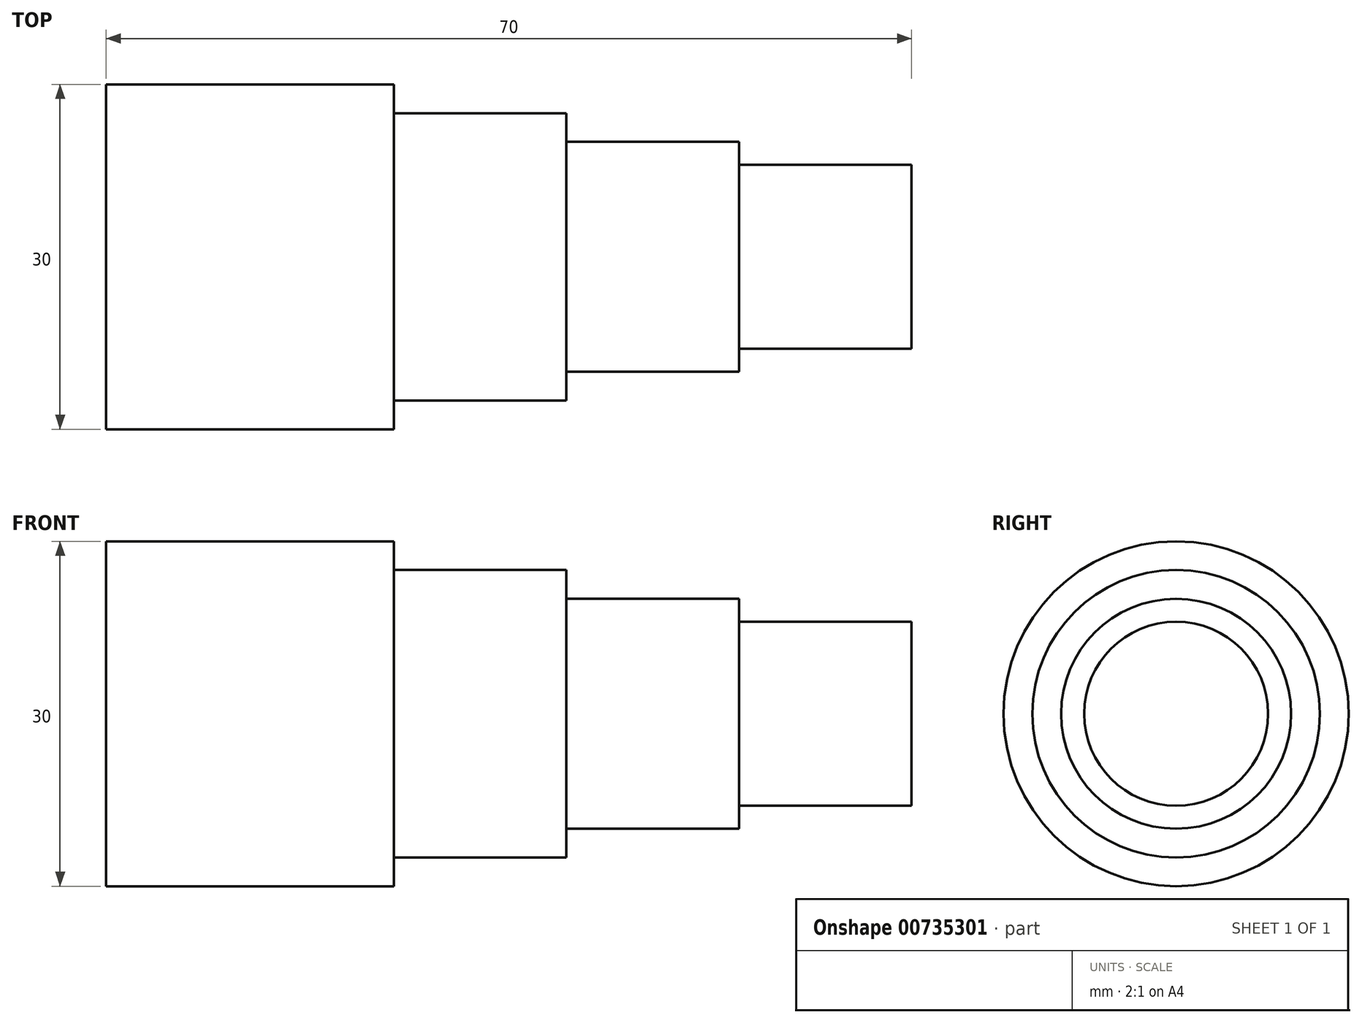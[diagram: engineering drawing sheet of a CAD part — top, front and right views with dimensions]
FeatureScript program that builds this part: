
annotation { "Feature Type Name" : "Feature", "Feature Type Description" : "" }
export const myFeature = defineFeature(function(context is Context, id is Id, definition is map)
    precondition{}
    {
        {
            var Q0;
            Q0=qCreatedBy(makeId("Right.planeOp"),FACE);
            var sketch = newSketch(context, id + "F0", { "sketchPlane" : qUnion([Q0])});
            skCircle(sketch, "E0", {"center": v(0, 0) * mm, "radius": 15 * mm});
            skSolve(sketch);
        }
        {
            var Q0;
            Q0=makeQuery(id+"F0.imprint","IMPRINT",FACE,{"disambiguationData":[TD([[makeQuery(id+"F0.imprint","IMPRINT",EDGE,{"derivedFrom":sQuery(id+"F0.wireOp",EDGE,"E0")}),1.0]])]});
            extrude(context, id + "F1", {"entities" : qUnion([Q0]), "oppositeDirection" : true, "depth" : 25 * mm, "offsetDistance" : 25 * mm});
        }
        {
            var Q0;
            Q0=makeQuery(id+"F1.opExtrude","CAP_FACE",FACE,{"disambiguationData":[OSD([sQuery(id+"F0.wireOp",EDGE,"E0")])],"isStart":true});
            var sketch = newSketch(context, id + "F2", { "sketchPlane" : qUnion([Q0])});
            skCircle(sketch, "E1", {"center": v(0, 0) * mm, "radius": 12.5 * mm});
            skSolve(sketch);
        }
        {
            var Q0;
            Q0=makeQuery(id+"F2.imprint","IMPRINT",FACE,{"disambiguationData":[TD([[makeQuery(id+"F2.imprint","IMPRINT",EDGE,{"derivedFrom":sQuery(id+"F2.wireOp",EDGE,"E1")}),1.0]])]});
            extrude(context, id + "F3", {"entities" : qUnion([Q0]), "operationType" : NewBodyOperationType.ADD, "depth" : 15 * mm, "offsetDistance" : 25 * mm});
        }
        {
            var Q0;
            Q0=makeQuery(id+"F3.opExtrude","CAP_FACE",FACE,{"disambiguationData":[OSD([sQuery(id+"F2.wireOp",EDGE,"E1")])],"isStart":false});
            var sketch = newSketch(context, id + "F4", { "sketchPlane" : qUnion([Q0])});
            skCircle(sketch, "E2", {"center": v(0, 0) * mm, "radius": 10 * mm});
            skSolve(sketch);
        }
        {
            var Q0;
            Q0 = qSketchRegion(id + "F4", true);
            extrude(context, id + "F5", {"entities" : qUnion([Q0]), "operationType" : NewBodyOperationType.ADD, "depth" : 15 * mm, "offsetDistance" : 25 * mm});
        }
        {
            var Q0;
            Q0=makeQuery(id+"F5.opExtrude","CAP_FACE",FACE,{"disambiguationData":[OSD([sQuery(id+"F4.wireOp",EDGE,"E2")])],"isStart":false});
            var sketch = newSketch(context, id + "F6", { "sketchPlane" : qUnion([Q0])});
            skCircle(sketch, "E3", {"center": v(0, 0) * mm, "radius": 8 * mm});
            skSolve(sketch);
        }
        {
            var Q0;
            Q0 = qSketchRegion(id + "F6", true);
            extrude(context, id + "F7", {"entities" : qUnion([Q0]), "operationType" : NewBodyOperationType.ADD, "depth" : 15 * mm, "offsetDistance" : 25 * mm});
        }
        {
            var Q0;
            Q0=makeQuery(id+"F7.opExtrude","CAP_FACE",FACE,{"disambiguationData":[OSD([sQuery(id+"F6.wireOp",EDGE,"E3")])],"isStart":false});
            var sketch = newSketch(context, id + "F8", { "sketchPlane" : qUnion([Q0])});
            skCircle(sketch, "E4", {"center": v(0, 0) * mm, "radius": 6 * mm});
            skSolve(sketch);
        }
        {
            var Q0;
            Q0=sQuery(id+"F8.wireOp",EDGE,"E4");
            extrude(context, id + "F9", {"bodyType" : ToolBodyType.SURFACE, "surfaceEntities" : qUnion([Q0]), "depth" : 10 * mm, "offsetDistance" : 25 * mm});
        }
    });
